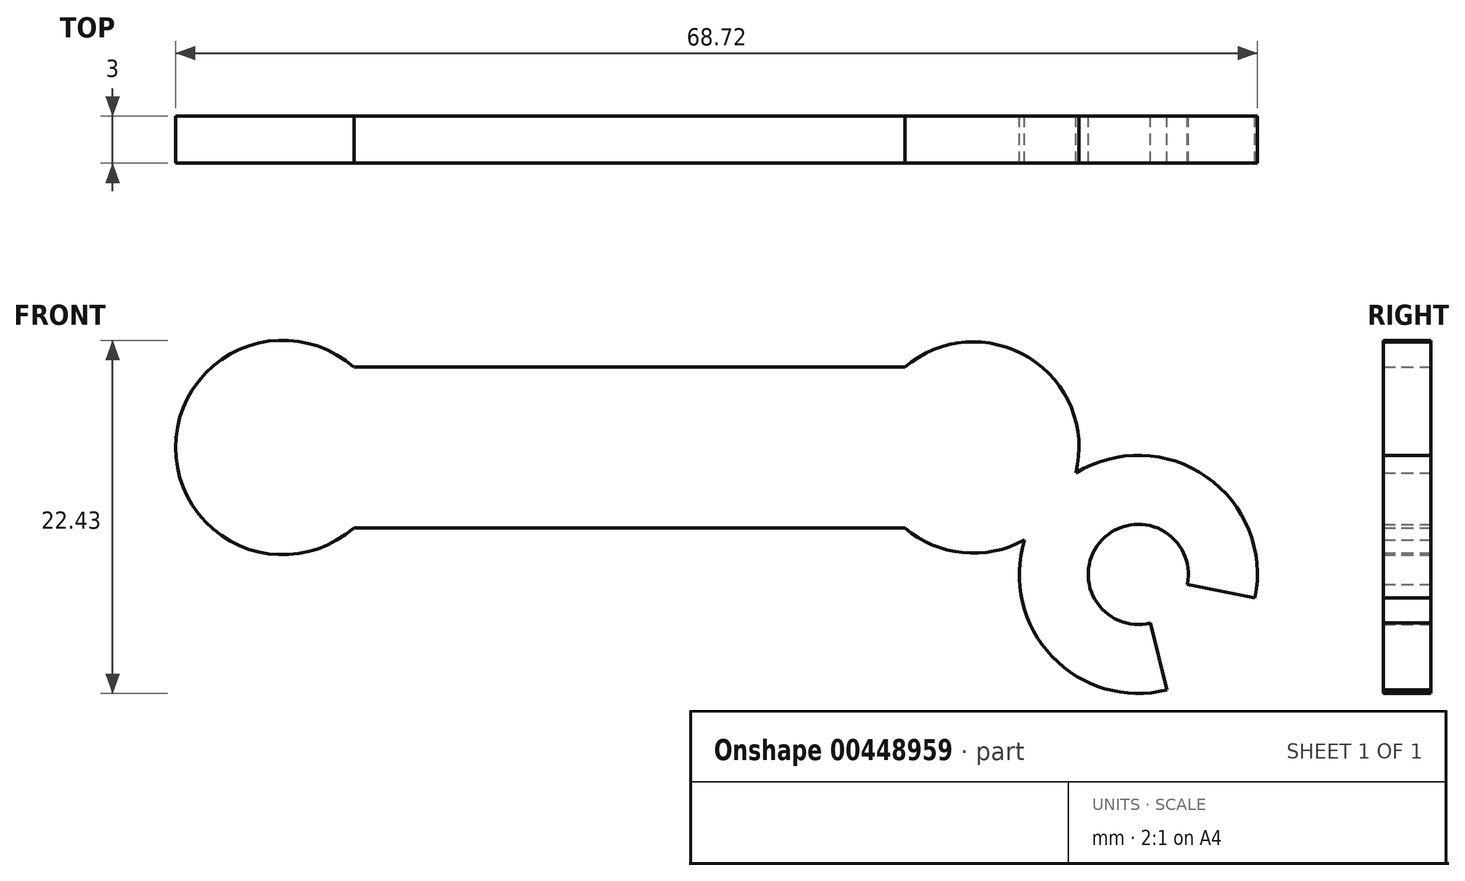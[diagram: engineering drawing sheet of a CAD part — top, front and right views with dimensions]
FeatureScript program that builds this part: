
annotation { "Feature Type Name" : "Feature", "Feature Type Description" : "" }
export const myFeature = defineFeature(function(context is Context, id is Id, definition is map)
    precondition{}
    {
        {
            var Q0;
            Q0=qCreatedBy(makeId("Front.planeOp"),FACE);
            var sketch = newSketch(context, id + "F0", { "sketchPlane" : qUnion([Q0])});
            skLineSegment(sketch, "E0", {"start": v(-24.64, -56.65) * mm, "end": v(11.9, -56.65) * mm});
            skLineSegment(sketch, "E1", {"start": v(11.9, -56.65) * mm, "end": v(11.9, -46.46) * mm});
            skLineSegment(sketch, "E2", {"start": v(11.9, -46.46) * mm, "end": v(-24.64, -46.46) * mm});
            skLineSegment(sketch, "E3", {"start": v(-24.64, -46.46) * mm, "end": v(-24.64, -56.65) * mm});
            skCircle(sketch, "E4", {"center": v(-28.34, -51.56) * mm, "radius": 6.81 * mm});
            skPoint(sketch, "E4.centerSnap0", {"position": v(-24.64, -51.56) * mm});
            skCircle(sketch, "E5", {"center": v(15.53, -51.56) * mm, "radius": 6.7 * mm});
            skPoint(sketch, "E5.centerSnap0", {"position": v(11.9, -51.56) * mm});
            skCircle(sketch, "E6", {"center": v(26, -59.62) * mm, "radius": 7.56 * mm});
            skSolve(sketch);
        }
        {
            var Q0;
            Q0 = qSketchRegion(id + "F0", true);
            extrude(context, id + "F1", {"entities" : qUnion([Q0]), "depth" : 3 * mm});
        }
        {
            var Q0;
            Q0=makeQuery(id+"F1.opExtrude","CAP_FACE",FACE,{"disambiguationData":[OSD([sQuery(id+"F0.wireOp",EDGE,"E0"),sQuery(id+"F0.wireOp",EDGE,"E2"),sQuery(id+"F0.wireOp",EDGE,"E4"),sQuery(id+"F0.wireOp",EDGE,"E5"),sQuery(id+"F0.wireOp",EDGE,"E6")])],"isStart":true});
            var sketch = newSketch(context, id + "F2", { "sketchPlane" : qUnion([Q0])});
            skCircle(sketch, "E7", {"center": v(-26, -59.62) * mm, "radius": 3.18 * mm});
            skLineSegment(sketch, "E8", {"start": v(-26, -59.62) * mm, "end": v(-39.7, -62.37) * mm});
            skLineSegment(sketch, "E9", {"start": v(-39.7, -62.37) * mm, "end": v(-29.1, -72.08) * mm});
            skLineSegment(sketch, "E10", {"start": v(-29.1, -72.08) * mm, "end": v(-26, -59.62) * mm});
            skSolve(sketch);
        }
        {
            var Q0;
            {var subQ0=sQuery(id+"F2.wireOp",EDGE,"E8");var subQ1=sQuery(id+"F2.wireOp",EDGE,"E7");var subQ2=makeQuery(id+"F2.imprint","INTERSECT",VERTEX,{"derivedFrom":[subQ1,subQ0]});Q0=makeQuery(id+"F2.imprint","IMPRINT",FACE,{"disambiguationData":[TD([[makeQuery(id+"F2.imprint","IMPRINT",EDGE,{"disambiguationData":[TD([[subQ2,-1.0]])],"derivedFrom":subQ1}),-1.0]])]});}
            var Q1;
            {var subQ0=sQuery(id+"F2.wireOp",EDGE,"E9");Q1=makeQuery(id+"F2.imprint","IMPRINT",FACE,{"disambiguationData":[TD([[makeQuery(id+"F2.imprint","IMPRINT",EDGE,{"derivedFrom":subQ0}),1.0]])]});}
            var Q2;
            {var subQ0=sQuery(id+"F2.wireOp",EDGE,"E8");var subQ1=sQuery(id+"F2.wireOp",EDGE,"E7");var subQ2=makeQuery(id+"F2.imprint","INTERSECT",VERTEX,{"derivedFrom":[subQ1,subQ0]});Q2=makeQuery(id+"F2.imprint","IMPRINT",FACE,{"disambiguationData":[TD([[makeQuery(id+"F2.imprint","IMPRINT",EDGE,{"disambiguationData":[TD([[subQ2,-1.0]])],"derivedFrom":subQ1}),1.0]])]});}
            var Q3;
            {var subQ0=sQuery(id+"F2.wireOp",EDGE,"E8");var subQ1=sQuery(id+"F2.wireOp",EDGE,"E7");var subQ2=makeQuery(id+"F2.imprint","INTERSECT",VERTEX,{"derivedFrom":[subQ1,subQ0]});Q3=makeQuery(id+"F2.imprint","IMPRINT",FACE,{"disambiguationData":[TD([[makeQuery(id+"F2.imprint","IMPRINT",EDGE,{"disambiguationData":[TD([[subQ2,1.0]])],"derivedFrom":subQ1}),1.0]])]});}
            var Q4;
            Q4 = qSketchRegion(id + "F4", true);
            var Q5;
            Q5 = qSketchRegion(id + "F5", true);
            extrude(context, id + "F3", {"entities" : qUnion([Q0, Q1, Q2, Q3, Q4, Q5]), "operationType" : NewBodyOperationType.REMOVE, "oppositeDirection" : true, "depth" : 25 * mm});
        }
    });
